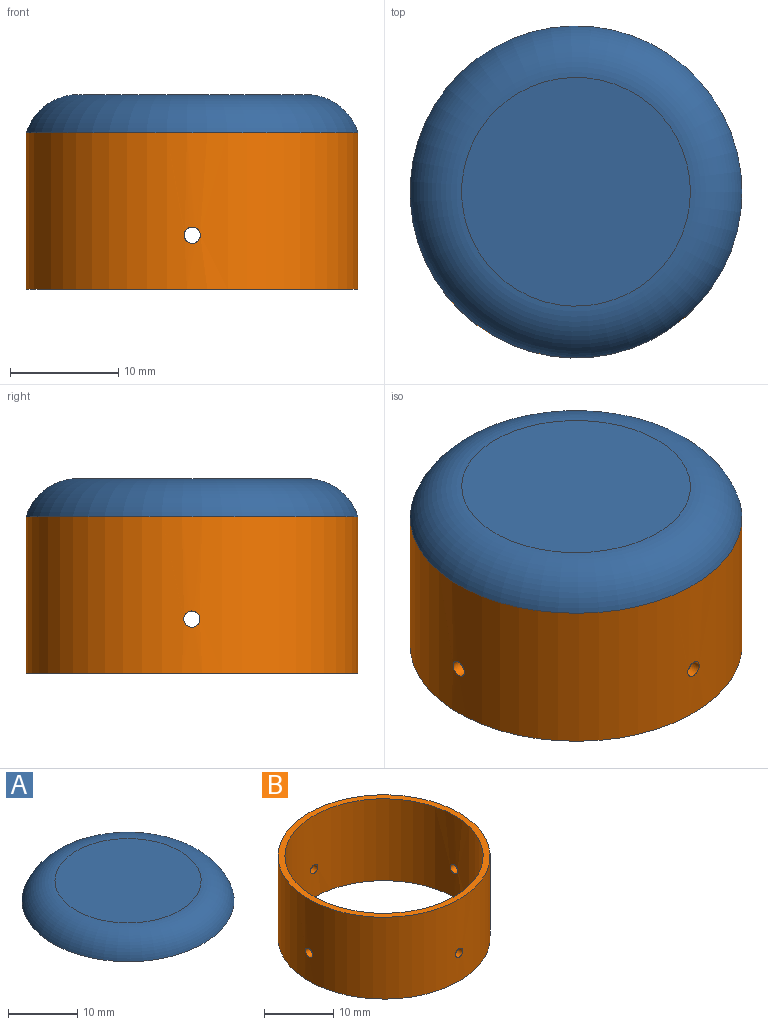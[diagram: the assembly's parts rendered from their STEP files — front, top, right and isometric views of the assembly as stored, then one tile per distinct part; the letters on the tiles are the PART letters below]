
ASSEMBLY  parts=2 mates=1
PART A: 3 faces, bbox 33.7x33.7x5 mm
  f0: plane 30.7x30.7mm, normal (0,0,-1), area 740.2mm2, adj f2
  f1: plane 21.16x21.16mm, normal (0,0,1), area 351.7mm2, adj f2
  f2: torus R=10.58mm, axis (0,0,-1), area 530.8mm2, adj f0,f1
PART B: 8 faces, bbox 30.7x30.7x14.5 mm
  f0: cylinder r=14.35mm len=28.7mm, axis (0,0,-1), area 1300.3mm2, adj f2,f3,f4,f5,f6,f7
  f1: cylinder r=15.35mm len=30.7mm, axis (0,0,-1), area 1391.4mm2, adj f2,f3,f4,f5,f6,f7
  f2: plane 30.7x30.7mm, normal (0,0,1), area 93.3mm2, adj f0,f1
  f3: plane 30.7x30.7mm, normal (0,0,-1), area 93.3mm2, adj f0,f1
  f4: cylinder r=0.75mm len=1.5mm, axis (1,0,0), area 4.7mm2, adj f0,f1
  f5: cylinder r=0.75mm len=1.5mm, axis (1,0,0), area 4.7mm2, adj f0,f1
  f6: cylinder r=0.75mm len=1.5mm, axis (0,-1,0), area 4.7mm2, adj f0,f1
  f7: cylinder r=0.75mm len=1.5mm, axis (0,-1,0), area 4.7mm2, adj f0,f1
PLACE A t=(-5.34,-4.27,24.08)mm
PLACE B t=(-5.34,-4.27,6.08)mm
MATE fastened B.f1 <-> A.f2  axis (0,0,-1) through (-5.34,-4.27,20.58)mm
